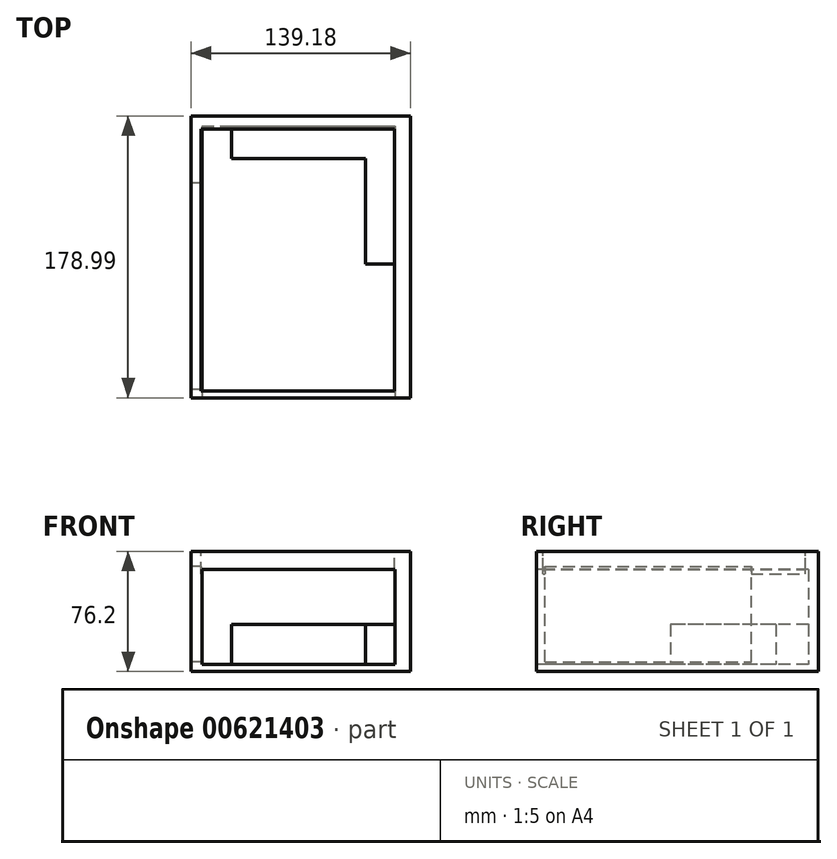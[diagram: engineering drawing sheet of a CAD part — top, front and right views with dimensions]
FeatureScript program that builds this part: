
annotation { "Feature Type Name" : "Feature", "Feature Type Description" : "" }
export const myFeature = defineFeature(function(context is Context, id is Id, definition is map)
    precondition{}
    {
        {
            var Q0;
            Q0=qCreatedBy(makeId("Top.planeOp"),FACE);
            var sketch = newSketch(context, id + "F0", { "sketchPlane" : qUnion([Q0])});
            skLineSegment(sketch, "E0.bottom", {"start": v(-71.94, 110.22) * mm, "end": v(67.24, 110.22) * mm});
            skLineSegment(sketch, "E0.top", {"start": v(-71.94, -68.77) * mm, "end": v(67.24, -68.77) * mm});
            skLineSegment(sketch, "E0.left", {"start": v(-71.94, 110.22) * mm, "end": v(-71.94, -68.77) * mm});
            skLineSegment(sketch, "E0.right", {"start": v(67.24, 110.22) * mm, "end": v(67.24, -68.77) * mm});
            skSolve(sketch);
        }
        {
            var Q0;
            Q0 = qSketchRegion(id + "F0", true);
            extrude(context, id + "F1", {"entities" : qUnion([Q0]), "depth" : 76.2 * mm, "offsetDistance" : 25.4 * mm});
        }
        {
            var Q0;
            Q0=makeQuery(id+"F1.opExtrude","SWEPT_FACE",FACE,{"disambiguationData":[OSD([sQuery(id+"F0.wireOp",EDGE,"E0.top")])]});
            var sketch = newSketch(context, id + "F2", { "sketchPlane" : qUnion([Q0])});
            skLineSegment(sketch, "E1.bottom", {"start": v(-65.06, 64.63) * mm, "end": v(57.46, 64.63) * mm});
            skLineSegment(sketch, "E1.top", {"start": v(-65.06, 4.38) * mm, "end": v(57.46, 4.38) * mm});
            skLineSegment(sketch, "E1.left", {"start": v(-65.06, 64.63) * mm, "end": v(-65.06, 4.38) * mm});
            skLineSegment(sketch, "E1.right", {"start": v(57.46, 64.63) * mm, "end": v(57.46, 4.38) * mm});
            skSolve(sketch);
        }
        {
            var Q0;
            Q0 = qSketchRegion(id + "F2", true);
            extrude(context, id + "F3", {"entities" : qUnion([Q0]), "operationType" : NewBodyOperationType.REMOVE, "oppositeDirection" : true, "depth" : 172.72 * mm, "offsetDistance" : 25.4 * mm});
        }
        {
            var Q0;
            Q0=makeQuery(id+"F1.opExtrude","SWEPT_FACE",FACE,{"disambiguationData":[OSD([sQuery(id+"F0.wireOp",EDGE,"E0.left")])]});
            var sketch = newSketch(context, id + "F4", { "sketchPlane" : qUnion([Q0])});
            skLineSegment(sketch, "E2.bottom", {"start": v(63.37, 6.03) * mm, "end": v(-67.77, 6.03) * mm});
            skLineSegment(sketch, "E2.top", {"start": v(63.37, 66.56) * mm, "end": v(-67.77, 66.56) * mm});
            skLineSegment(sketch, "E2.left", {"start": v(63.37, 6.03) * mm, "end": v(63.37, 66.56) * mm});
            skLineSegment(sketch, "E2.right", {"start": v(-67.77, 6.03) * mm, "end": v(-67.77, 66.56) * mm});
            skSolve(sketch);
        }
        {
            var Q0;
            Q0 = qSketchRegion(id + "F4", true);
            extrude(context, id + "F5", {"entities" : qUnion([Q0]), "operationType" : NewBodyOperationType.REMOVE, "oppositeDirection" : true, "depth" : 25.4 * mm, "offsetDistance" : 25.4 * mm});
        }
        {
            var Q0;
            Q0=makeQuery(id+"F3.boolean.opBoolean","COPY",FACE,{"derivedFrom":makeQuery(id+"F3.opExtrude","SWEPT_FACE",FACE,{"disambiguationData":[OSD([sQuery(id+"F2.wireOp",EDGE,"E1.top")])]})});
            var sketch = newSketch(context, id + "F6", { "sketchPlane" : qUnion([Q0])});
            skLineSegment(sketch, "E3", {"start": v(-46.5, 103.95) * mm, "end": v(-46.5, 83.28) * mm});
            skLineSegment(sketch, "E4", {"start": v(-46.5, 83.28) * mm, "end": v(38.85, 83.28) * mm});
            skLineSegment(sketch, "E5", {"start": v(38.85, 83.28) * mm, "end": v(38.85, 16.33) * mm});
            skLineSegment(sketch, "E6", {"start": v(38.85, 16.33) * mm, "end": v(57.46, 16.33) * mm});
            skLineSegment(sketch, "E7", {"start": v(57.46, 16.33) * mm, "end": v(57.46, 103.95) * mm});
            skLineSegment(sketch, "E8", {"start": v(57.46, 103.95) * mm, "end": v(-46.5, 103.95) * mm});
            skSolve(sketch);
        }
        {
            var Q0;
            Q0 = qSketchRegion(id + "F6", true);
            extrude(context, id + "F7", {"entities" : qUnion([Q0]), "operationType" : NewBodyOperationType.ADD, "depth" : 25.4 * mm, "offsetDistance" : 25.4 * mm});
        }
        {
            var Q0;
            Q0=makeQuery(id+"F1.opExtrude","CAP_FACE",FACE,{"disambiguationData":[OSD([sQuery(id+"F0.wireOp",EDGE,"E0.bottom"),sQuery(id+"F0.wireOp",EDGE,"E0.top"),sQuery(id+"F0.wireOp",EDGE,"E0.left"),sQuery(id+"F0.wireOp",EDGE,"E0.right")])],"isStart":false});
            var sketch = newSketch(context, id + "F8", { "sketchPlane" : qUnion([Q0])});
            skLineSegment(sketch, "E9.bottom", {"start": v(-65.64, 102.16) * mm, "end": v(57.19, 102.16) * mm});
            skLineSegment(sketch, "E9.top", {"start": v(-65.64, -64.5) * mm, "end": v(57.19, -64.5) * mm});
            skLineSegment(sketch, "E9.left", {"start": v(-65.64, 102.16) * mm, "end": v(-65.64, -64.5) * mm});
            skLineSegment(sketch, "E9.right", {"start": v(57.19, 102.16) * mm, "end": v(57.19, -64.5) * mm});
            skSolve(sketch);
        }
        {
            var Q0;
            Q0 = qSketchRegion(id + "F8", true);
            extrude(context, id + "F9", {"entities" : qUnion([Q0]), "operationType" : NewBodyOperationType.REMOVE, "oppositeDirection" : true, "depth" : 14.22 * mm, "offsetDistance" : 25.4 * mm});
        }
    });
